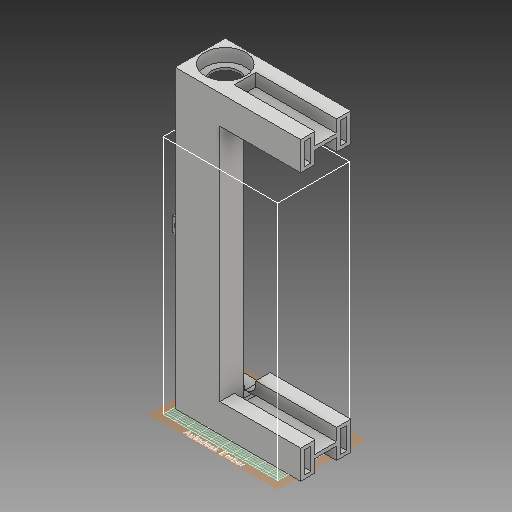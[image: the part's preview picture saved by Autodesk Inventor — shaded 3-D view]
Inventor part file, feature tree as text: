
AUTODESK INVENTOR PART (.ipt)
format: ipt  version: 2018 (Build 220112000, 112)  size: 602,624 bytes
history: native  units: mm
features: extrude x18, sketch x18, fillet x4
ambient origin geometry x8: Origin, YZ Plane, XZ Plane, XY Plane, X Axis, Y Axis, Z Axis, Center Point
bodies: Solid1 (feature_tree)
feature tree (40):
  extrude  "Extrusion1"  Depth=165.0mm
  extrude  "Extrusion2"  Depth=8.5mm
  extrude  "Extrusion3"  Depth=25.0mm TaperAngle=0.0deg
  extrude  "Extrusion4"  Depth=22.75mm
  extrude  "Extrusion5"  Depth=7.1mm
  extrude  "Extrusion6"  Depth=7.1mm TaperAngle=0.0deg
  fillet  "Fillet1"  Radius=5.0mm
  extrude  "Extrusion7"  Depth=10.0mm TaperAngle=0.0deg
  fillet  "Fillet2"  Radius=2.0mm
  extrude  "Extrusion8"  Depth=8.0mm
  extrude  "Extrusion9"  Depth=16.0mm
  fillet  "Fillet3"  Radius=8.0mm
  extrude  "Extrusion10"  Depth=6.0mm
  extrude  "Extrusion11"  Depth=12.25mm
  fillet  "Fillet4"  Radius=12.25mm
  extrude  "Extrusion12"  Depth=12.25mm
  extrude  "Extrusion13"  Depth=12.25mm
  extrude  "Extrusion14"  Depth=40.0mm
  sketch  "Sketch16"  dims[d40=2.0mm d41=8.0mm]
  extrude  "Extrusion15"  Depth=8.0mm
  extrude  "Extrusion16"  Depth=2.0mm
  extrude  "Extrusion17"  Depth=6.0mm
  extrude  "Extrusion18"  Depth=165.0mm
  sketch  "Sketch1"  dims[d0=25.0mm d1=165.0mm]
  sketch  "Sketch2"  dims[d2=3.0mm d3=0.0mm d4=8.5mm]
  sketch  "Sketch3"  dims[d5=8.5mm d6=25.0mm d7=0.0mm]
  sketch  "Sketch4"  dims[d8=25.0mm d9=22.75mm]
  sketch  "Sketch5"  dims[d10=7.1mm d11=0.0mm d12=15.5mm]
  sketch  "Sketch6"  dims[d13=165.0mm d14=0.0mm d15=7.1mm d16=0.0mm d17=5.0mm]
  sketch  "Sketch7"  dims[d18=5.0mm d19=10.0mm d20=0.0mm d21=2.0mm]
  sketch  "Sketch8"  dims[d22=16.0mm d23=8.0mm]
  sketch  "Sketch9"  dims[d24=16.0mm d25=16.0mm d26=8.0mm]
  sketch  "Sketch10"  dims[d27=45.0mm d28=0.0mm d29=6.0mm]
  sketch  "Sketch11"  dims[d30=12.25mm d31=3.5mm d32=12.25mm]
  sketch  "Sketch13"  dims[d33=3.5mm d34=12.25mm]
  sketch  "Sketch14"  dims[d35=12.25mm d36=3.5mm]
  sketch  "Sketch15"  dims[d37=40.0mm d38=0.0mm d39=1.0mm]
  sketch  "Sketch17"  dims[d42=1.0mm d43=2.0mm]
  sketch  "Sketch18"  dims[d44=12.0mm d45=0.0mm d46=6.0mm]
  sketch  "Sketch19"  dims[d47=6.0mm d48=4.0mm d49=8.0mm d50=6.5mm d51=0.0mm d52=6.35mm d53=8.0mm d54=0.0mm d55=6.5mm d56=47.0mm d57=1.0mm d58=7.0mm d59=0.0mm d60=7.1mm d61=0.0mm d62=14.5mm d63=0.0mm d64=2.0mm d65=0.0mm d66=8.5mm d67=2.0mm d68=0.0mm d69=20.0mm d70=0.0mm d71=165.0mm d72=0.0mm]
